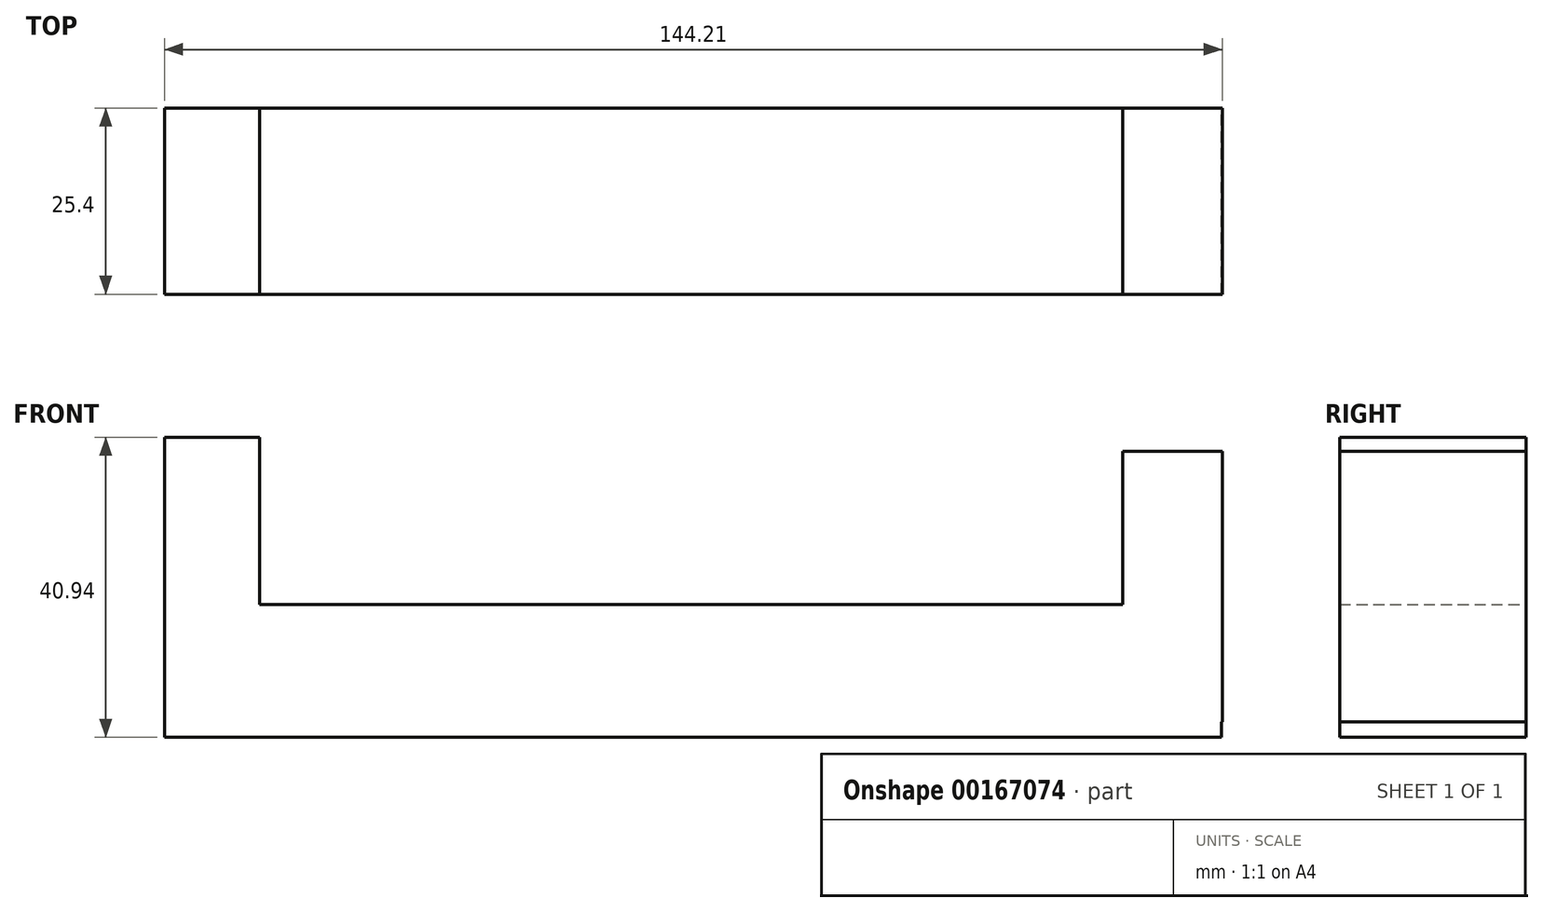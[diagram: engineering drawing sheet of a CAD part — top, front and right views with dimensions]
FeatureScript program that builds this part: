
annotation { "Feature Type Name" : "Feature", "Feature Type Description" : "" }
export const myFeature = defineFeature(function(context is Context, id is Id, definition is map)
    precondition{}
    {
        {
            var Q0;
            Q0=qCreatedBy(makeId("Front.planeOp"),FACE);
            var sketch = newSketch(context, id + "F0", { "sketchPlane" : qUnion([Q0])});
            skLineSegment(sketch, "E0.bottom", {"start": v(-77.84, -46.84) * mm, "end": v(77.84, -46.84) * mm});
            skLineSegment(sketch, "E0.top", {"start": v(-77.84, -68.2) * mm, "end": v(77.84, -68.2) * mm});
            skLineSegment(sketch, "E0.left", {"start": v(-77.84, -46.84) * mm, "end": v(-77.84, -68.2) * mm});
            skLineSegment(sketch, "E0.right", {"start": v(77.84, -46.84) * mm, "end": v(77.84, -68.2) * mm});
            skPoint(sketch, "E0.middle", {"position": v(0, -57.52) * mm});
            skLineSegment(sketch, "E1.bottom", {"start": v(-12.5, 26.78) * mm, "end": v(12.5, 26.78) * mm});
            skLineSegment(sketch, "E1.top", {"start": v(-12.5, -67.71) * mm, "end": v(12.5, -67.71) * mm});
            skLineSegment(sketch, "E1.left", {"start": v(-12.5, 26.78) * mm, "end": v(-12.5, -67.71) * mm});
            skLineSegment(sketch, "E1.right", {"start": v(12.5, 26.78) * mm, "end": v(12.5, -67.71) * mm});
            skPoint(sketch, "E1.middle", {"position": v(0, -20.47) * mm});
            skLineSegment(sketch, "E2.bottom", {"start": v(-72.06, 45.22) * mm, "end": v(72.06, 45.22) * mm});
            skLineSegment(sketch, "E2.top", {"start": v(-72.06, 27.1) * mm, "end": v(72.06, 27.1) * mm});
            skLineSegment(sketch, "E2.left", {"start": v(-72.06, 45.22) * mm, "end": v(-72.06, 27.1) * mm});
            skLineSegment(sketch, "E2.right", {"start": v(72.06, 45.22) * mm, "end": v(72.06, 27.1) * mm});
            skPoint(sketch, "E2.middle", {"position": v(0, 36.16) * mm});
            skLineSegment(sketch, "E3.bottom", {"start": v(-72.06, 68.04) * mm, "end": v(-59.11, 68.04) * mm});
            skLineSegment(sketch, "E3.top", {"start": v(-72.06, 43.77) * mm, "end": v(-59.11, 43.77) * mm});
            skLineSegment(sketch, "E3.left", {"start": v(-72.06, 68.04) * mm, "end": v(-72.06, 43.77) * mm});
            skLineSegment(sketch, "E3.right", {"start": v(-59.11, 68.04) * mm, "end": v(-59.11, 43.77) * mm});
            skPoint(sketch, "E3.middle", {"position": v(-65.59, 55.9) * mm});
            skLineSegment(sketch, "E4.bottom", {"start": v(58.56, 66.1) * mm, "end": v(72.15, 66.1) * mm});
            skLineSegment(sketch, "E4.top", {"start": v(58.56, 29.2) * mm, "end": v(72.15, 29.2) * mm});
            skLineSegment(sketch, "E4.left", {"start": v(58.56, 66.1) * mm, "end": v(58.56, 29.2) * mm});
            skLineSegment(sketch, "E4.right", {"start": v(72.15, 66.1) * mm, "end": v(72.15, 29.2) * mm});
            skPoint(sketch, "E4.middle", {"position": v(65.35, 47.65) * mm});
            skSolve(sketch);
        }
        {
            var Q0;
            Q0 = qSketchRegion(id + "F0", true);
            extrude(context, id + "F1", {"entities" : qUnion([Q0]), "depth" : 25.4 * mm});
        }
        {
            var Q0;
            Q0=qCreatedBy(makeId("Right.planeOp"),FACE);
            var sketch = newSketch(context, id + "F2", { "sketchPlane" : qUnion([Q0])});
            skLineSegment(sketch, "E5.bottom", {"start": v(-880.7, -46.68) * mm, "end": v(171.28, -46.68) * mm});
            skLineSegment(sketch, "E5.top", {"start": v(-880.7, -91.01) * mm, "end": v(171.28, -91.01) * mm});
            skLineSegment(sketch, "E5.left", {"start": v(171.28, -46.68) * mm, "end": v(171.28, -91.01) * mm});
            skLineSegment(sketch, "E5.right", {"start": v(-880.7, -46.68) * mm, "end": v(-880.7, -91.01) * mm});
            skPoint(sketch, "E5.middle", {"position": v(-354.71, -68.85) * mm});
            skSolve(sketch);
        }
        {
            var Q0;
            Q0 = qSketchRegion(id + "F2", true);
            extrude(context, id + "F3", {"entities" : qUnion([Q0]), "operationType" : NewBodyOperationType.ADD, "depth" : 25.4 * mm});
        }
        {
            var Q0;
            Q0 = qSketchRegion(id + "F2", true);
            extrude(context, id + "F4", {"entities" : qUnion([Q0]), "operationType" : NewBodyOperationType.ADD, "depth" : 25.4 * mm});
        }
        {
            var Q0;
            Q0=makeQuery(id+"F1.opExtrude","SWEPT_BODY",BODY,{"disambiguationData":[OSD([sQuery(id+"F0.wireOp",EDGE,"E0.bottom"),sQuery(id+"F0.wireOp",EDGE,"E0.top"),sQuery(id+"F0.wireOp",EDGE,"E0.left"),sQuery(id+"F0.wireOp",EDGE,"E0.right"),sQuery(id+"F0.wireOp",EDGE,"E1.bottom"),sQuery(id+"F0.wireOp",EDGE,"E1.left"),sQuery(id+"F0.wireOp",EDGE,"E1.right")])]});
            deleteBodies(context, id + "F5", {"entities" : qUnion([Q0])});
        }
    });
